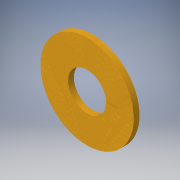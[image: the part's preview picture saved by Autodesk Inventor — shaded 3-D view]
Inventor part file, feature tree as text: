
AUTODESK INVENTOR PART (.ipt)
format: ipt  version: 2016 (Build 200138000, 138)  size: 98,816 bytes
history: native  units: in
note: dims shown in document units (in); Inventor stores cm internally (conversion verified against a paired STEP export)
features: extrude x1, sketch x1
ambient origin geometry x8: Origin, YZ Plane, XZ Plane, XY Plane, X Axis, Y Axis, Z Axis, Center Point
bodies: Solid1 (feature_tree)
feature tree (2):
  extrude  "Extrusion1"  Depth=0.0394in
  sketch  "Sketch1"  dims[d0=0.6378in d1=0.2598in d2=0.0394in d3=0.0in]
